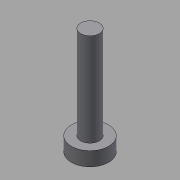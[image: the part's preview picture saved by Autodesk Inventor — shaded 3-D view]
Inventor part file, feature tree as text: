
AUTODESK INVENTOR PART (.ipt)
format: ipt  version: 2015 (Build 190159000, 159)  size: 80,384 bytes
history: native  units: mm
features: extrude x3, sketch x3
ambient origin geometry x8: Origin, YZ Plane, XZ Plane, XY Plane, X Axis, Y Axis, Z Axis, Center Point
bodies: Solid1 (feature_tree)
feature tree (6):
  extrude  "Extrusion1"  Depth=2.0mm TaperAngle=0.0deg
  extrude  "Extrusion2"  Depth=10.0mm TaperAngle=0.0deg
  extrude  "Extrusion3"  Depth=1.0mm
  sketch  "Sketch1"  dims[d0=2.0mm d1=2.0mm d2=0.0mm]
  sketch  "Sketch2"  dims[d3=1.0mm d4=10.0mm d5=0.0mm]
  sketch  "Sketch3"  dims[d6=2.0mm d7=1.0mm d8=1.0mm d9=0.0mm]
